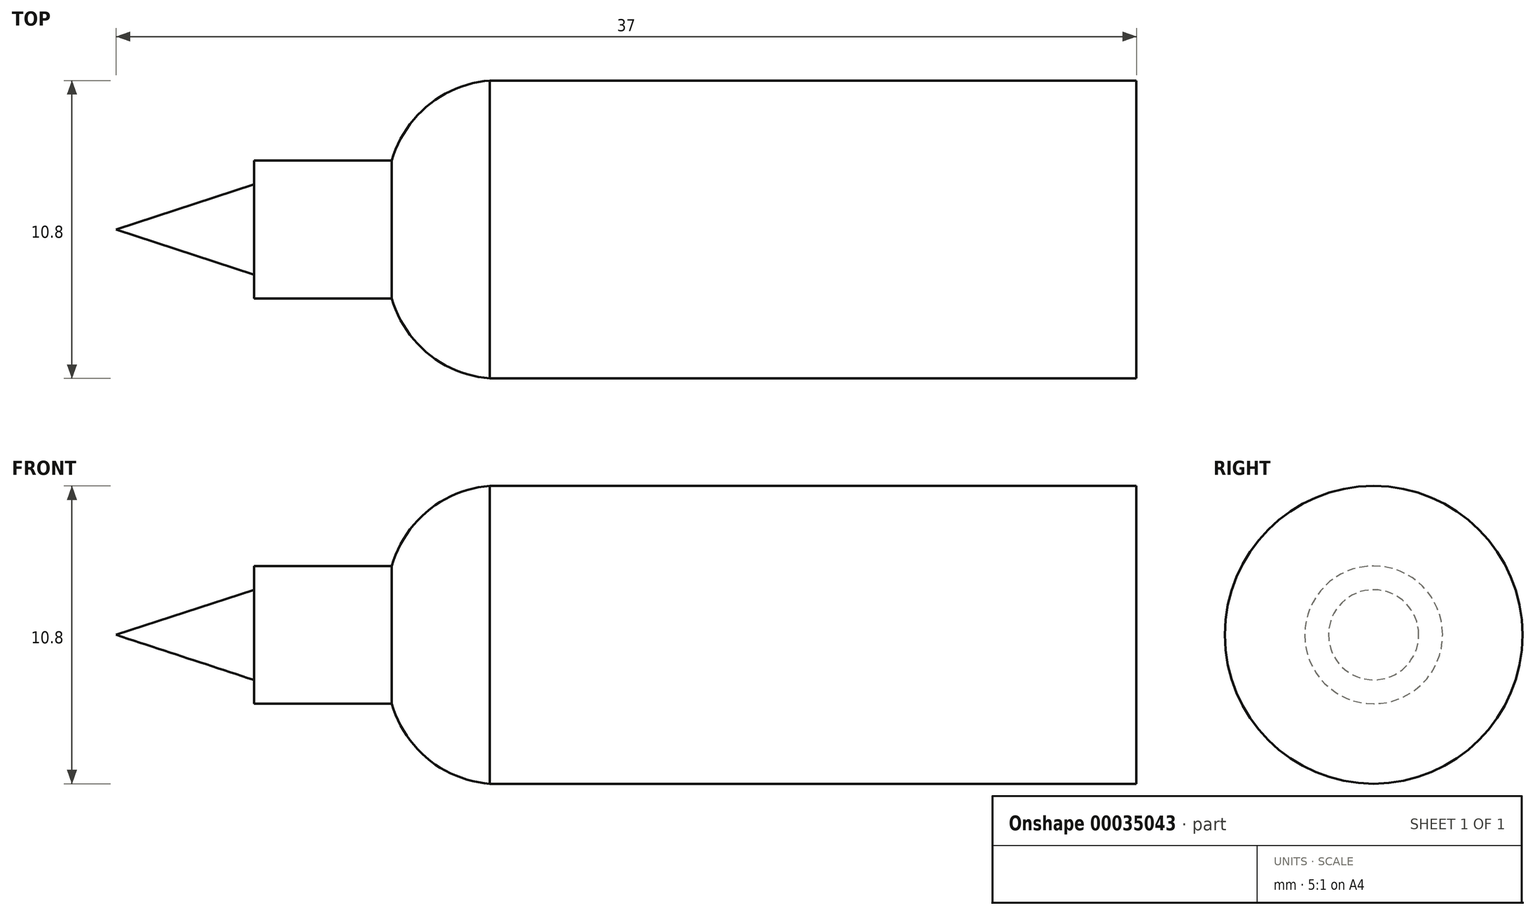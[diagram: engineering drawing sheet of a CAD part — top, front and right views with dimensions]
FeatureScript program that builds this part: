
annotation { "Feature Type Name" : "Feature", "Feature Type Description" : "" }
export const myFeature = defineFeature(function(context is Context, id is Id, definition is map)
    precondition{}
    {
        {
            var Q0;
            Q0=qCreatedBy(makeId("Front.planeOp"),FACE);
            var sketch = newSketch(context, id + "F0", { "sketchPlane" : qUnion([Q0])});
            skLineSegment(sketch, "E0", {"start": v(-108.25, 0) * mm, "end": v(-145.25, 0) * mm});
            skLineSegment(sketch, "E1.0", {"start": v(-140.25, 1.64) * mm, "end": v(-140.25, 2.5) * mm});
            skLineSegment(sketch, "E2.0", {"start": v(-108.25, 0) * mm, "end": v(-108.25, 5.4) * mm});
            skLineSegment(sketch, "E3.0", {"start": v(-108.25, 5.4) * mm, "end": v(-131.7, 5.4) * mm});
            skLineSegment(sketch, "E4.0", {"start": v(-135.25, 2.5) * mm, "end": v(-140.25, 2.5) * mm});
            skLineSegment(sketch, "E5", {"start": v(-145.25, 0) * mm, "end": v(-140.25, 1.64) * mm});
            skPoint(sketch, "E6.visualSharp", {"position": v(-135.25, 5.4) * mm});
            skArc(sketch, "E7", {"start": v(-131.7, 5.4) * mm, "mid": v(-133.93, 4.5) * mm, "end": v(-135.25, 2.5) * mm});
            skSolve(sketch);
        }
        {
            var Q0;
            Q0 = qSketchRegion(id + "F0", true);
            var Q1;
            Q1=sQuery(id+"F0.wireOp",EDGE,"E0");
            revolve(context, id + "F1", {"entities" : qUnion([Q0]), "axis" : qUnion([Q1]), "revolveType" : RevolveType.FULL});
        }
    });
